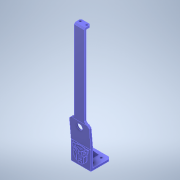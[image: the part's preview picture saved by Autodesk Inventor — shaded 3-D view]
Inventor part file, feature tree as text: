
AUTODESK INVENTOR PART (.ipt)
format: ipt  version: 2022.6 (Build 266554000, 554)  size: 658,944 bytes
history: native  units: mm
features: extrude x6, hole x4, sketch x4, other x3, chamfer x2, rib x1, mirror x1, projected_geometry x1
ambient origin geometry x8: Origin, YZ Plane, XZ Plane, XY Plane, X Axis, Y Axis, Z Axis, Center Point
bodies: Solid1 (feature_tree)
feature tree (22):
  extrude  "Extrusion1"  Depth=30.0mm
  extrude  "Extrusion2"  Depth=3.0mm
  hole  "Mounting Holes"  [1 undecoded]
  rib  "Rib1"
  mirror  "Mirror1"
  other  "Bend Part1"
  hole  "Camera Mounting Holes"  [1 undecoded]
  chamfer  "Chamfer1"  Distance=3.0mm
  extrude  "Decepticon Logo"  Depth=3.0mm
  extrude  "Autobots Logo"  Depth=3.0mm TaperAngle=0.0deg
  extrude  "Compass Mount"  Depth=15.0mm
  extrude  "Extrusion7"  Depth=10.0mm
  hole  "Compass Mount Holes"  [1 undecoded]
  chamfer  "Chamfer3"  Distance=22.0mm
  hole  "Hole4"  [1 undecoded]
  sketch  "Sketch8"  dims[d0=30.0mm d1=30.0mm]
  other  "Image1"
  sketch  "Sketch10"  dims[d2=3.0mm d3=0.0mm d4=21.0mm]
  other  "Image2"
  sketch  "Sketch12"  dims[d5=13.0mm]
  sketch  "Sketch17"  dims[d7=2.4mm d8=6.0mm d9=4.0mm d10=2.0mm d11=90.0deg d12=6.0mm d13=0.0mm d15=30.0mm d16=30.0mm d17=3.0mm d18=3.0mm d19=3.0mm d20=0.0mm d21=15.0mm d22=13.5mm d23=7.0mm d24=3.4mm d25=6.0mm d26=4.0mm d27=2.0mm d28=90.0deg d29=6.0mm d30=0.0mm d31=22.0mm d35=1.0mm d36=2.0mm d37=0.0mm d38=0.0mm d39=1.0mm d40=1.0mm d41=27.0mm d42=32.0mm d43=3.0mm d44=2.0mm d45=45.0deg d71=2.0mm d72=0.0mm d157=1.5mm d158=0.0mm d162=3.0mm d163=0.872665mm d164=4.0mm d167=125.0mm d168=15.0mm d169=0.0mm d170=7.0mm d171=3.0mm d172=0.0mm d173=2.0mm d174=2.0mm d175=45.0deg d176=9.5mm d177=3.4mm d178=6.0mm d179=4.0mm d180=2.0mm d181=90.0deg d182=8.0mm d183=20.594885mm d184=3.0mm d185=2.0mm d186=45.0deg d188=28.0mm d192=8.0mm d193=8.6mm d194=6.0mm d195=15.9mm d196=1.2mm d197=90.0deg d198=10.0mm d199=20.594885mm d73=0.5mm d74=0.872665mm]
  projected_geometry  "Projected Loop2"
note: 4 required parameter values undecoded (feature->parameter linkage not recoverable at this tier; creation-order binding heuristic only, values carry confidence <= 0.55)
